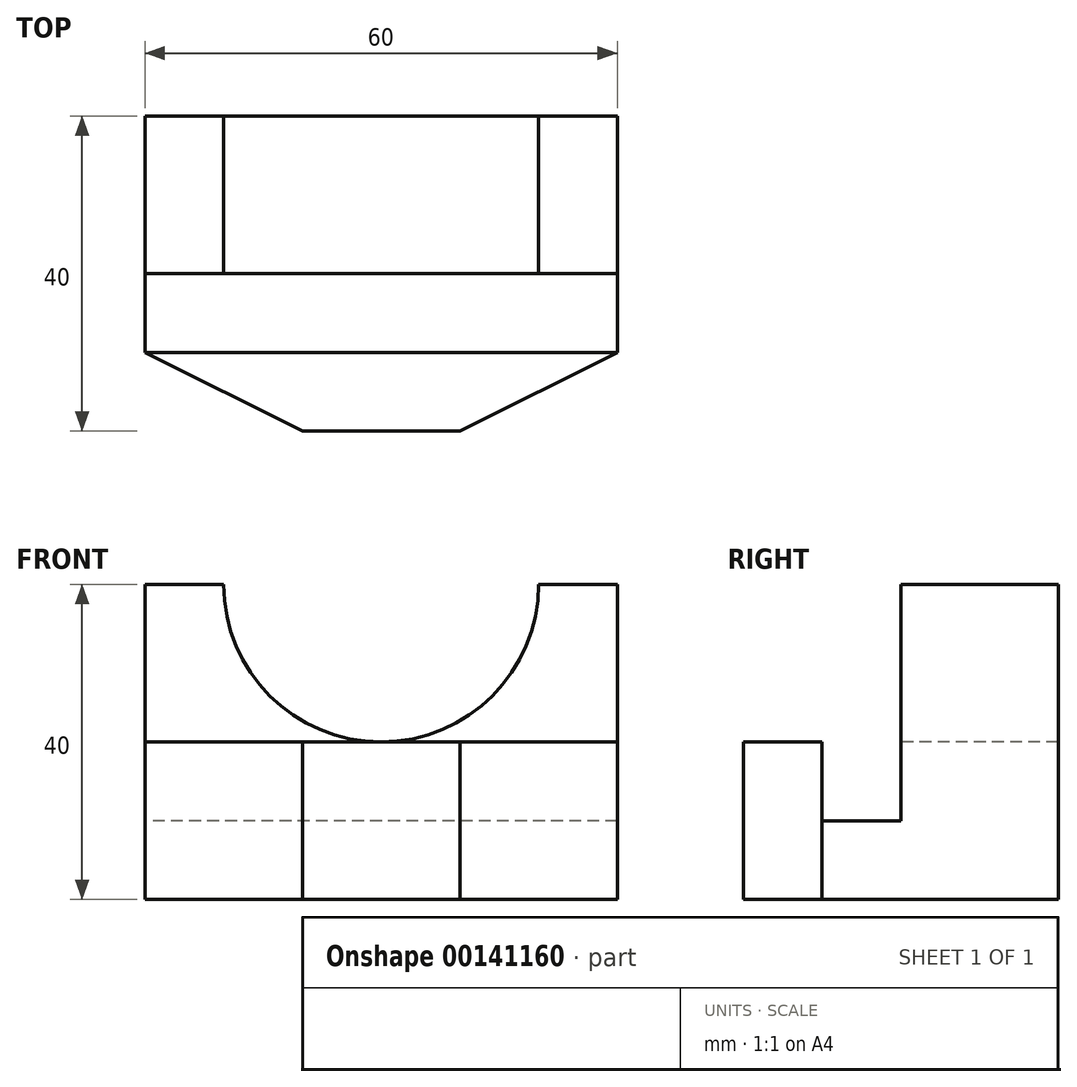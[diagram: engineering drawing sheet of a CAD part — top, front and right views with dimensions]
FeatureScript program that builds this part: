
annotation { "Feature Type Name" : "Feature", "Feature Type Description" : "" }
export const myFeature = defineFeature(function(context is Context, id is Id, definition is map)
    precondition{}
    {
        {
            var Q0;
            Q0=qCreatedBy(makeId("Right.planeOp"),FACE);
            var sketch = newSketch(context, id + "F0", { "sketchPlane" : qUnion([Q0])});
            skLineSegment(sketch, "E0.bottom", {"start": v(0, 0) * mm, "end": v(40, 0) * mm});
            skLineSegment(sketch, "E0.top", {"start": v(20, 40) * mm, "end": v(40, 40) * mm});
            skLineSegment(sketch, "E0.left", {"start": v(0, 0) * mm, "end": v(0, 20) * mm});
            skLineSegment(sketch, "E0.right", {"start": v(40, 0) * mm, "end": v(40, 40) * mm});
            skLineSegment(sketch, "E1", {"start": v(0, 20) * mm, "end": v(10, 20) * mm});
            skLineSegment(sketch, "E2", {"start": v(10, 20) * mm, "end": v(10, 10) * mm});
            skLineSegment(sketch, "E3", {"start": v(10, 10) * mm, "end": v(20, 10) * mm});
            skLineSegment(sketch, "E4", {"start": v(20, 10) * mm, "end": v(20, 40) * mm});
            skSolve(sketch);
        }
        {
            var Q0;
            Q0=makeQuery(id+"F0.imprint","IMPRINT",FACE,{"disambiguationData":[TD([[makeQuery(id+"F0.imprint","IMPRINT",EDGE,{"derivedFrom":sQuery(id+"F0.wireOp",EDGE,"E0.bottom")}),1.0]])]});
            extrude(context, id + "F1", {"entities" : qUnion([Q0]), "endBound" : BoundingType.SYMMETRIC, "depth" : 60 * mm});
        }
        {
            var Q0;
            Q0=makeQuery(id+"F1.opExtrude","SWEPT_FACE",FACE,{"disambiguationData":[OSD([sQuery(id+"F0.wireOp",EDGE,"E1")])]});
            var sketch = newSketch(context, id + "F2", { "sketchPlane" : qUnion([Q0])});
            skLineSegment(sketch, "E5.0", {"start": v(30, 10) * mm, "end": v(-30, 10) * mm});
            skLineSegment(sketch, "E5.1", {"start": v(30, 0) * mm, "end": v(-30, 0) * mm});
            skLineSegment(sketch, "E5.2", {"start": v(30, 0) * mm, "end": v(30, 10) * mm});
            skLineSegment(sketch, "E5.3", {"start": v(-30, 0) * mm, "end": v(-30, 10) * mm});
            skLineSegment(sketch, "E6", {"start": v(-30, 10) * mm, "end": v(-10, 0) * mm});
            skLineSegment(sketch, "E7", {"start": v(30, 10) * mm, "end": v(10, 0) * mm});
            skSolve(sketch);
        }
        {
            var Q0;
            {var subQ0=sQuery(id+"F2.wireOp",EDGE,"E5.3");Q0=makeQuery(id+"F2.imprint","IMPRINT",FACE,{"disambiguationData":[TD([[makeQuery(id+"F2.imprint","IMPRINT",EDGE,{"derivedFrom":subQ0}),-1.0]])]});}
            var Q1;
            {var subQ0=sQuery(id+"F2.wireOp",EDGE,"E5.2");Q1=makeQuery(id+"F2.imprint","IMPRINT",FACE,{"disambiguationData":[TD([[makeQuery(id+"F2.imprint","IMPRINT",EDGE,{"derivedFrom":subQ0}),1.0]])]});}
            extrude(context, id + "F3", {"entities" : qUnion([Q0, Q1]), "operationType" : NewBodyOperationType.REMOVE, "endBound" : BoundingType.THROUGH_ALL, "oppositeDirection" : true, "depth" : 25 * mm});
        }
        {
            var Q0;
            Q0=makeQuery(id+"F1.opExtrude","SWEPT_FACE",FACE,{"disambiguationData":[OSD([sQuery(id+"F0.wireOp",EDGE,"E4")])]});
            var sketch = newSketch(context, id + "F4", { "sketchPlane" : qUnion([Q0])});
            skArc(sketch, "E8", {"start": v(-20, 40) * mm, "mid": v(0, 20) * mm, "end": v(20, 40) * mm});
            skLineSegment(sketch, "E9.0", {"start": v(30, 40) * mm, "end": v(-30, 40) * mm});
            skSolve(sketch);
        }
        {
            var Q0;
            {var subQ0=sQuery(id+"F4.wireOp",EDGE,"E8");Q0=makeQuery(id+"F4.imprint","IMPRINT",FACE,{"disambiguationData":[TD([[makeQuery(id+"F4.imprint","IMPRINT",EDGE,{"derivedFrom":subQ0}),1.0]])]});}
            extrude(context, id + "F5", {"entities" : qUnion([Q0]), "operationType" : NewBodyOperationType.REMOVE, "endBound" : BoundingType.THROUGH_ALL, "oppositeDirection" : true, "depth" : 25 * mm});
        }
    });
